# Revit family: Comfort D Shape Ribbed Countertop Basin 1TH
name_source: partatom
category: Plumbing Fixtures
units: mm (PartAtom-declared; Revit-internal decimal feet)

## family parameters
Always vertical = Yes
Cut with Voids When Loaded = No
Enable Cutting in Views = No
Maintain Annotation Orientation = No
OmniClass Number = 23.45.00.00
OmniClass Title = Sanitary, Laundry, and Cleaning Equipment
Part Type = Normal
Room Calculation Point = No
Round Connector Dimension = Use Diameter
Shared = No
Work Plane-Based = No

## types (1)
- Comfort D Shape Ribbed Countertop Basin 1TH
    Category = Basins - Countertop
    Ceramic = Ceramic
    Colour = White
    Default Elevation = 0 mm  [stored 0 ft]
    Manufacturer = Lecico SA
    Material = Vitreous China
    Model = Comfort D Shape Ribbed Countertop Basin 1TH
    Product Code = COMBASCTO1DSHBC
    Silver = Silver
    Technical Dimensions = W400 x H140 x D350mm
    URL = https://www.lecicosa.co.za

note: [stored X ft] marks values corroborated as IEEE doubles in the binary element streams (Revit-internal decimal feet)

## geometry (parser evidence)
native form markers: Sweep x1
no freeform markers — native parametric forms only
